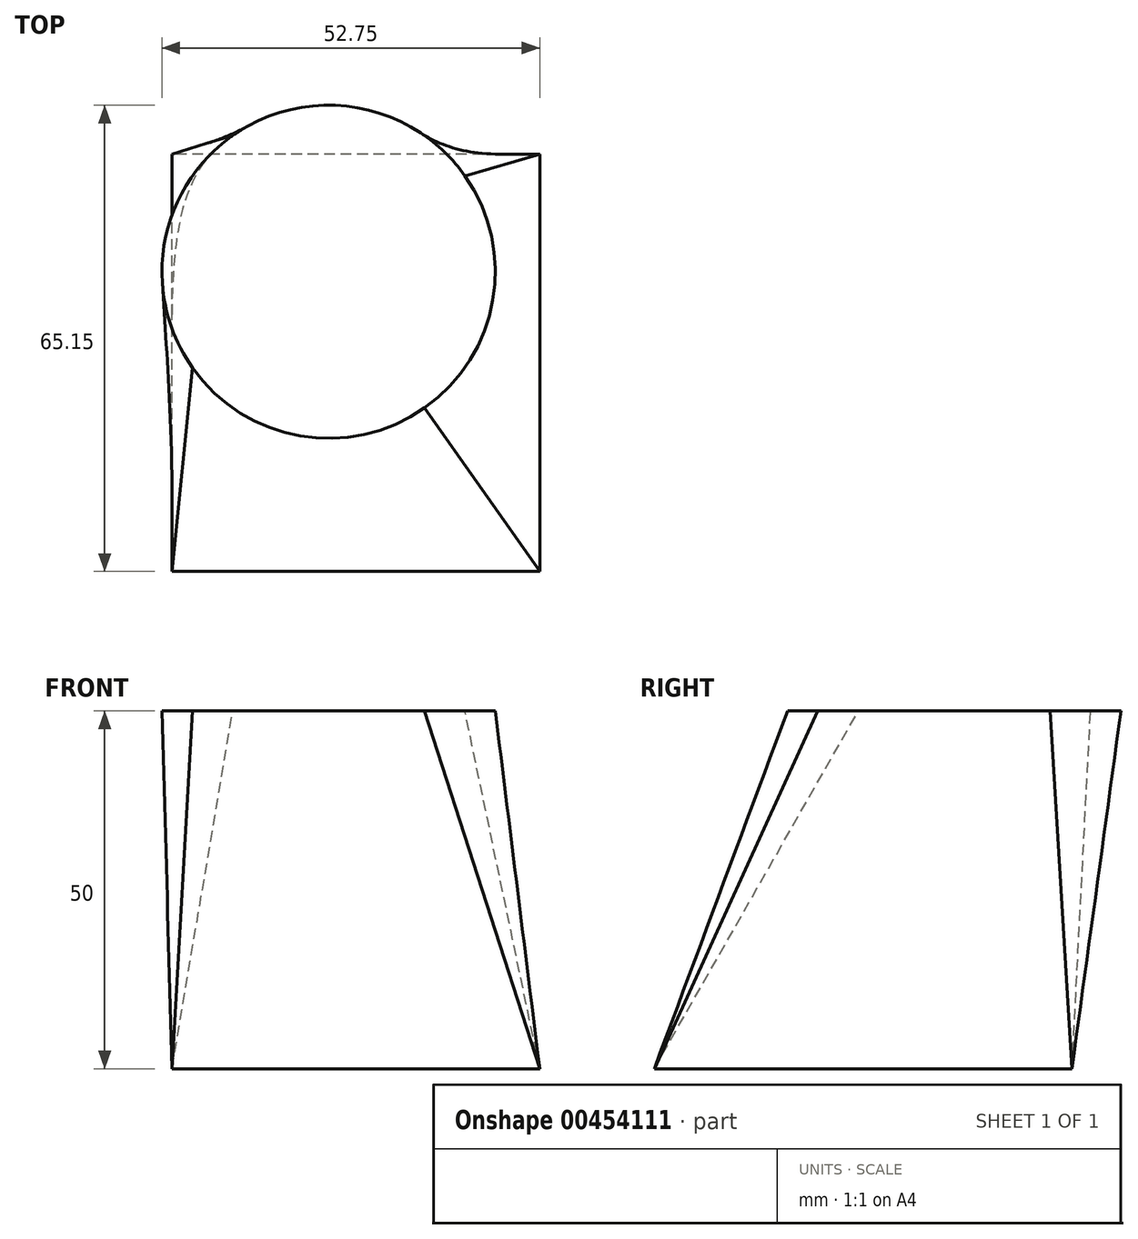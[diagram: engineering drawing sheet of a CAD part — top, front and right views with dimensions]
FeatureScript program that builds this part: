
annotation { "Feature Type Name" : "Feature", "Feature Type Description" : "" }
export const myFeature = defineFeature(function(context is Context, id is Id, definition is map)
    precondition{}
    {
        {
            var Q0;
            Q0=qCreatedBy(makeId("Top.planeOp"),FACE);
            var sketch = newSketch(context, id + "F0", { "sketchPlane" : qUnion([Q0])});
            skLineSegment(sketch, "E0.bottom", {"start": v(0, 0) * mm, "end": v(-51.34, 0) * mm});
            skLineSegment(sketch, "E0.top", {"start": v(0, 58.32) * mm, "end": v(-51.34, 58.32) * mm});
            skLineSegment(sketch, "E0.left", {"start": v(0, 0) * mm, "end": v(0, 58.32) * mm});
            skLineSegment(sketch, "E0.right", {"start": v(-51.34, 0) * mm, "end": v(-51.34, 58.32) * mm});
            skSolve(sketch);
        }
        {
            var Q0;
            Q0=qCreatedBy(makeId("Top.planeOp"),FACE);
            cPlane(context, id + "F1", {"entities" : qUnion([Q0]), "cplaneType" : CPlaneType.OFFSET, "offset" : 50 * mm, "width" : 150 * mm, "height" : 150 * mm});
        }
        {
            var Q0;
            Q0=qCreatedBy(id+"F1.planeOp",FACE);
            var sketch = newSketch(context, id + "F2", { "sketchPlane" : qUnion([Q0])});
            skCircle(sketch, "E1", {"center": v(-29.48, 41.88) * mm, "radius": 23.27 * mm});
            skSolve(sketch);
        }
        {
            var Q0;
            Q0 = qSketchRegion(id + "F0", true);
            var Q1;
            Q1 = qSketchRegion(id + "F2", true);
            loft(context, id + "F3", {"sheetProfilesArray" : [{ "sheetProfileEntities" : qUnion([Q0]) }, { "sheetProfileEntities" : qUnion([Q1]) }]});
        }
    });
